# Revit family: IS_CeraSprint_B9761_BIM_NL
name_source: partatom
category: Plumbing Fixtures
revit_build: Autodesk Revit 2017 (Build: 20171027_0315(x64)
units: mm (PartAtom-declared; Revit-internal decimal feet)

## family parameters
Cut with Voids When Loaded = No
Host = Face
OmniClass Number = 23.45.55.17
OmniClass Title = Mixing Faucets
Part Type = Normal
Room Calculation Point = No
Round Connector Dimension = Use Diameter
Shared = Yes

## types (1)
- B9761AA - CERASPRINT FONTEINKRAAN 5L KW
    Accessories = www.idealstandardnederland.nl
    AreaUnits = millimeters
    Assembly Code = C1030200
    AssetType = Vast
    BIMObjectName = CERASPRINT FONTEINKRAAN 5L KW
    BREEAMApproved = No
    BarCode = 3800861034032
    Brand = Ideal Standard
    CWFU = 0
    CodePerformance = DIN 4109
    Color = Chrome
    ConnectionType = Sanitair
    Cost = 0 $
    Default Elevation = 800 mm  [stored 2.62467 ft]
    Description = CeraSprint toiletkraan DN 15. Vaste gegoten uitloop. Straalregelaar. Sprong 86 mm. Hoogte uitloop 35 mm. Onderbevestiging (met aansluiting G1/2"). Cartouche met keramische schijven. Geluidsniveau volgens norm DIN 4109, Groep 1.
    DurationUnit = jaar
    ECA = No
    ExpectedLife = 25
    FaucetFunction = MIXED
    FaucetOperation = LEVERHANDLE
    FaucetType = PILLAR
    Features = Toiletkraan DN 15. Vaste gegoten uitloop. Straalregelaar. Sprong 86 mm. Hoogte uitloop 35 mm. Onderbevestiging (met aansluiting G1/2"). Cartouche met keramische schijven. Geluidsniveau volgens norm DIN 4109, Groep 1.
    Finish = Chroom
    HWFU = 0
    IfcExportAs = IfcValveType
    IfcExportType = FAUCET
    InstallationInstructions = https://www.idealstandardnederland.nl
    LinearUnits = millimeters
    ManufacturerURL = http://www.idealstandardnederland.nl
    Material = Brass
    Model = B9761AA
    ModelNumber = B9761AA
    ModelReference = CeraSprint toiletkraan DN 15. Vaste gegoten uitloop. Straalregelaar. Sprong 86 mm. Hoogte uitloop 35 mm. Onderbevestiging (met aansluiting G1/2"). Cartouche met keramische schijven. Geluidsniveau volgens norm DIN 4109, Groep 1.
    NBSReference = 45-35-70/???
    Name = CERASPRINT FONTEINKRAAN 5L KW
    NettWeight = 0,87 kg
    NominalHeight = 120 mm
    NominalLength = 124 mm
    NominalWidth = 44 mm
    ProductInformation = http://www.idealstandardnederland.nl
    Reference = CERASPRINT FONTEINKRAAN 5L KW
    Shape = Gesculptuurd
    Size = 44 x 124 x 120 mm
    Space = Intern
    SpareParts = www.idealstandardnederland.nl
    TMV3 = No
    TestPressure = 10 Bar
    URL = www.idealstandardnederland.nl
    ValveMechanism = Keramische schijven
    ValveOperation = Eenhendel
    Version = 2
    VolumeUnits = liter
    WFU = 0
    WRAS = No
    WarrantyDescription = Fabrieksgarantie
    WarrantyDurationParts = 10
    WarrantyDurationUnit = jaar
    WaterEfficientProduct = No
    WorkingPressure = 1-5 bar

note: [stored X ft] marks values corroborated as IEEE doubles in the binary element streams (Revit-internal decimal feet)

## geometry (parser evidence)
native form markers: Sweep x4
no freeform markers — native parametric forms only
